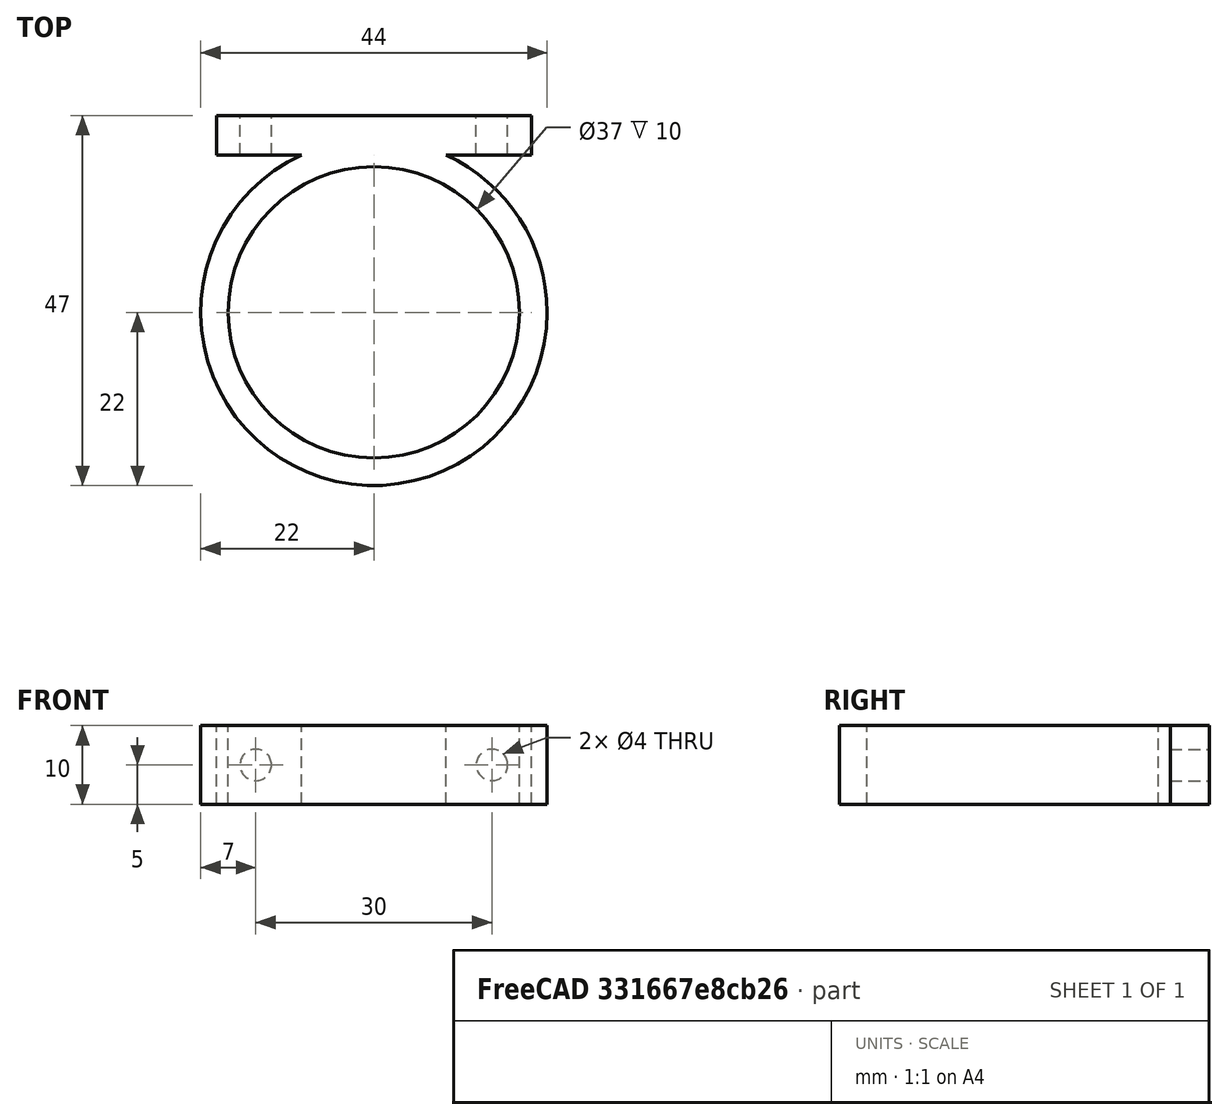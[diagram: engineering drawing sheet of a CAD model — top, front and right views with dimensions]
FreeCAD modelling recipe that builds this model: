
FCSTD DOCUMENT  (FreeCAD 0.17R13522 (Git))
Label: attachment-motor
License: All rights reserved
LicenseURL: http://en.wikipedia.org/wiki/All_rights_reserved
objects: Part::Cylinder×4, Part::MultiFuse×2, Part::Box×1, Part::Cut×1
note: 8 computed .brp shape members not serialized (recipe doc carries the construction recipe); baked Part::Feature solids carry a one-line shape summary decoded from their .brp

FEATURE [Part::Cylinder] Cylinder
  Angle = 360
  AttacherType = Attacher::AttachEngine3D
  Height = 10
  Placement = pos=(0,0,-5) rot=(0,0,1;0rad)
  Radius = 22
FEATURE [Part::Cylinder] Cylinder001
  Angle = 360
  AttacherType = Attacher::AttachEngine3D
  Height = 10
  Placement = pos=(0,0,-5) rot=(0,0,1;0rad)
  Radius = 18.5
FEATURE [Part::Box] Box  label="Cube"
  AttacherType = Attacher::AttachEngine3D
  Height = 10
  Length = 40
  Placement = pos=(-20,20,-5) rot=(0,0,1;0rad)
  Width = 5
FEATURE [Part::MultiFuse] Fusion  label="Positive Fusion"
  Shapes = -> [Cylinder,Box]
FEATURE [Part::Cylinder] Cylinder002
  Angle = 360
  AttacherType = Attacher::AttachEngine3D
  Height = 10
  Placement = pos=(15,20,0) rot=(1,0,0;4.71239rad)
  Radius = 2
FEATURE [Part::Cylinder] Cylinder003
  Angle = 360
  AttacherType = Attacher::AttachEngine3D
  Height = 10
  Placement = pos=(-15,20,0) rot=(-1,0,0;1.5708rad)
  Radius = 2
FEATURE [Part::MultiFuse] Fusion001  label="Negative Fusion"
  Shapes = -> [Cylinder003,Cylinder002,Cylinder001]
FEATURE [Part::Cut] Cut
  Base = -> Fusion
  Tool = -> Fusion001
